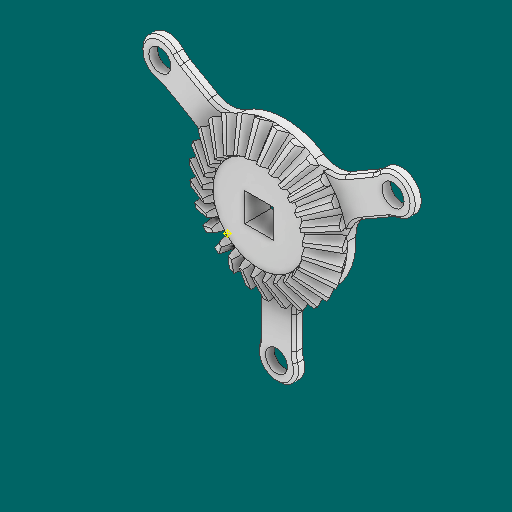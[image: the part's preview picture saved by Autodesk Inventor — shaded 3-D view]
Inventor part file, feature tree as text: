
AUTODESK INVENTOR PART (.ipt)
format: ipt  version: 2023.1 (Build 271208000, 208)  size: 777,728 bytes
history: native  units: mm
features: other x24, pattern_circular x3, sketch x3, loft x2, extrude x2, fillet x1, chamfer x1
ambient origin geometry x6: Origin, XZ Plane, X Axis, Y Axis, Z Axis, Center Point
bodies: Solid1 (feature_tree)
feature tree (36):
  other  "Top Point"
  other  "Mesh Plane2"
  other  "Teeth Body"
  other  "Start Point"
  other  "Tooth Plane"
  other  "Start Sketch"
  other  "End Point"
  other  "3D Sketch Right"
  other  "End Plane Right"
  loft  "Loft Right"
  pattern_circular  "Circular Pattern Right"  [2 undecoded]
  other  "3D Sketch Left"
  other  "End Plane Left"
  loft  "Loft Left"
  pattern_circular  "Circular Pattern Left"  [2 undecoded]
  other  "Fix Body"
  extrude  "Extrusion1"  Depth=5.08mm
  fillet  "Fillet1"  Radius=31.06566mm
  pattern_circular  "Circular Pattern4"  [2 undecoded]
  extrude  "Extrusion2"  Depth=5.08mm
  chamfer  "Chamfer1"  Distance=6.192895mm
  other  "Mesh Plane"
  other  "Top Plane"
  other  "Teeth Body Sketch"
  other  "End Plane"
  other  "End Sketch"
  other  "Helical Curve Left"
  other  "End Sketch Left"
  other  "Body Sketch"
  sketch  "Sketch6"  dims[d0=34.29mm d1=32.736122mm]
  other  "Srf1"
  other  "Helical Curve Right"
  other  "End Sketch Right"
  sketch  "Sketch8"  dims[d2=35.584898mm]
  sketch  "Sketch9"  dims[d3=6.985mm d4=9.06743mm d5=90.0deg d7=9.009874mm d8=9.638731mm d9=31.06566mm d11=7.1247mm d12=5.788854mm d15=6.192895mm d16=19.95972mm d17=0.0mm d18=90.0deg d19=0.0mm d20=90.0deg d21=270.0mm d22=360.0deg d26=144.697709mm d27=3.632189mm d28=34.29mm d29=-10.358413mm d30=5.788854mm d31=6.192895mm d32=19.95972mm d35=0.0mm d37=0.0mm d39=0.0mm d40=90.0deg d41=270.0mm d42=360.0deg d46=90.0deg d47=90.0deg d48=0.0mm d49=0.0mm d50=90.0deg d51=1.163553mm d52=0.0mm d53=0.0mm d54=0.0mm d56=5.887559mm d57=35.738878mm d58=31.771398mm d59=22.962267mm d60=20.413157mm d61=22.962267mm d62=20.413157mm d63=90.0deg d64=90.0deg d65=144.697709mm d66=31.5mm d67=34.29mm d68=-10.358413mm d69=3.632189mm d70=6.192895mm d71=19.95972mm d72=5.788854mm d73=20.413157mm d74=22.962267mm d75=0.0mm d76=90.0deg d77=0.0mm d78=90.0deg d79=0.0mm d80=90.0deg d81=270.0mm d82=360.0deg d84=10.0mm d85=20.0mm d86=20.0mm d87=10.0mm d88=0.0mm d89=0.0mm d90=5.08mm d91=62.23mm d92=30.0mm d94=360.0deg d96=2.0mm d97=7.9375mm d98=30.0mm d100=360.0deg d102=2.0mm d103=0.0mm d104=6.35mm d105=30.0mm d106=360.0deg d108=6.604mm d109=6.604mm d110=0.0mm d111=0.0mm d112=0.6mm d113=3.175mm d114=45.0deg]
  other  "Pitch Diameter"
note: 6 required parameter values undecoded (feature->parameter linkage not recoverable at this tier; creation-order binding heuristic only, values carry confidence <= 0.55)
